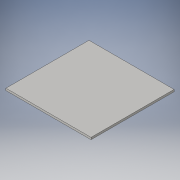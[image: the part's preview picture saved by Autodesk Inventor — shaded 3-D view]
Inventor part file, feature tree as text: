
AUTODESK INVENTOR PART (.ipt)
format: ipt  version: 2016 (Build 200138000, 138)  size: 86,528 bytes
history: native  units: in
note: dims shown in document units (in); Inventor stores cm internally (conversion verified against a paired STEP export)
features: extrude x1, sketch x1
ambient origin geometry x8: Origin, YZ Plane, XZ Plane, XY Plane, X Axis, Y Axis, Z Axis, Center Point
bodies: Body1 (feature_tree)
feature tree (2):
  extrude  "Extrusion2"  Depth=5.125in
  sketch  "Sketch1"  dims[d0=5.0in d1=5.125in d4=0.125in d5=0.0in]
